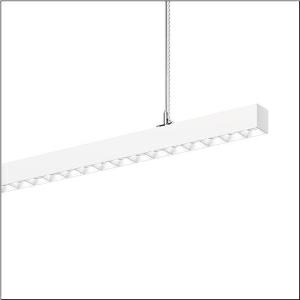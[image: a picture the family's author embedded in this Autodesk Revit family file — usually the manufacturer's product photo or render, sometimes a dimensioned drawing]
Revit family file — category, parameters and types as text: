
# Revit family: silica_r__21_51mx36dc4dwb_53ae
name_source: partatom
category: Lighting Fixtures
units: mm (PartAtom-declared; Revit-internal decimal feet)

## family parameters
Cut with Voids When Loaded = No
Host = Face
Light Source = No
Part Type = Normal
Room Calculation Point = No
Round Connector Dimension = Use Diameter
Shared = No

## types (1)
- --- (1 x LED, 17650 lm, 97.4 W, 4000K)
    Apparent Load = 97 VA
    CIE Flux Codes = 83 98 100 61 100
    Color Rendering = 80
    Color Temperature = 4000K
    Default Elevation = 1800 mm
    Description = Silica® 21, office luminaire, primary light control with darklight reflector, of PMMA, white, CAT 2 (L<= 3000cd/m²), light emission: direct/indirect distribution, primary light characteristic: symmetric, installation type: suspended mounting, LED, rated luminous flux: 17.650lm, luminous efficacy: 181lm/W, light colour: 840, colour temperature: 4000K, with terminal, 3+2-pole, max. 2.5mm², mains connection: 220..240V, AC, 50/60Hz, rated input power: 97.4W, luminaire housing, of aluminium, traffic white (RAL 9016), length: 3.004mm, width: 53mm, height: 53mm, protection rating (complete): IP20, insulation class (complete): insulation class I (protective earthing), certification: CE, permissible operating ambient temperature: 0..+35°C, standard: EN 50419, packaging unit: 1 piece
    Height = 53 mm
    Lamp = 1 x LED
    Lamp Light Flux = 17650 lm
    Lamp Power = 97.4 W
    Lamp count = 1
    Length = 3004 mm
    Luminous efficacy = 181 lm/W
    Manufacturer = Siteco
    ModVariant = No
    Model = 51MX36DC4DWB
    Mounting Place = Ceiling
    Mounting Type = Pendant
    Number of Poles = 1
    OnlyDefault = Yes
    Power Factor = 1
    Product Name = Silica® 21
    Product group = office luminaire | ceiling pendant
    ProductGroupID = 902
    Protection Class = Protection class I
    Protection Degree = IP 20
    RLX_Detail_Level = 1
    RLX_Emergency_Light_Flux = 0 lm
    RLX_Emergency_Type = 0
    RLX_Emergency_Type_DB = No
    RlxData = <blob elided: 60933 chars, md5=f660efc1>
    Socket = socket
    Standby Power = 0 W
    System Light Flux = 17650 lm
    System Power = 97 W
    Type Comments = factory setting: luminous flux: 100 % | dim-lin: 254 | 336 mA
    Type Image = l_1313634.jpg
    URL = http://relux.com
    VarID = @adj_070333
    Voltage = 0 V
    Weight = 0.00 kg
    Width = 53 mm

## geometry (parser evidence)
native form markers: Blend x4, Sweep x15
no freeform markers — native parametric forms only
